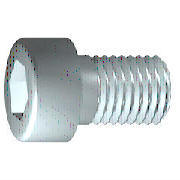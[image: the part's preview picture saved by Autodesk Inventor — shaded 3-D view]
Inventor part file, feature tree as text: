
AUTODESK INVENTOR PART (.ipt)
format: ipt  version: 2024.3 (Build 283343000, 343)  size: 192,512 bytes
history: native  units: mm (DEFAULTED — no unit token found)
features: extrude x1, plane x1, fillet x1
ambient origin geometry x7: Origin, YZ Plane, XY Plane, X Axis, Y Axis, Z Axis, Center Point
bodies: Solid1 (feature_tree), Body (feature_tree)
feature tree (3):
  extrude  "Slot"  Depth=18.0mm
  plane  "Work Plane1"
  fillet  "Fillet2"  Radius=0.49086mm
